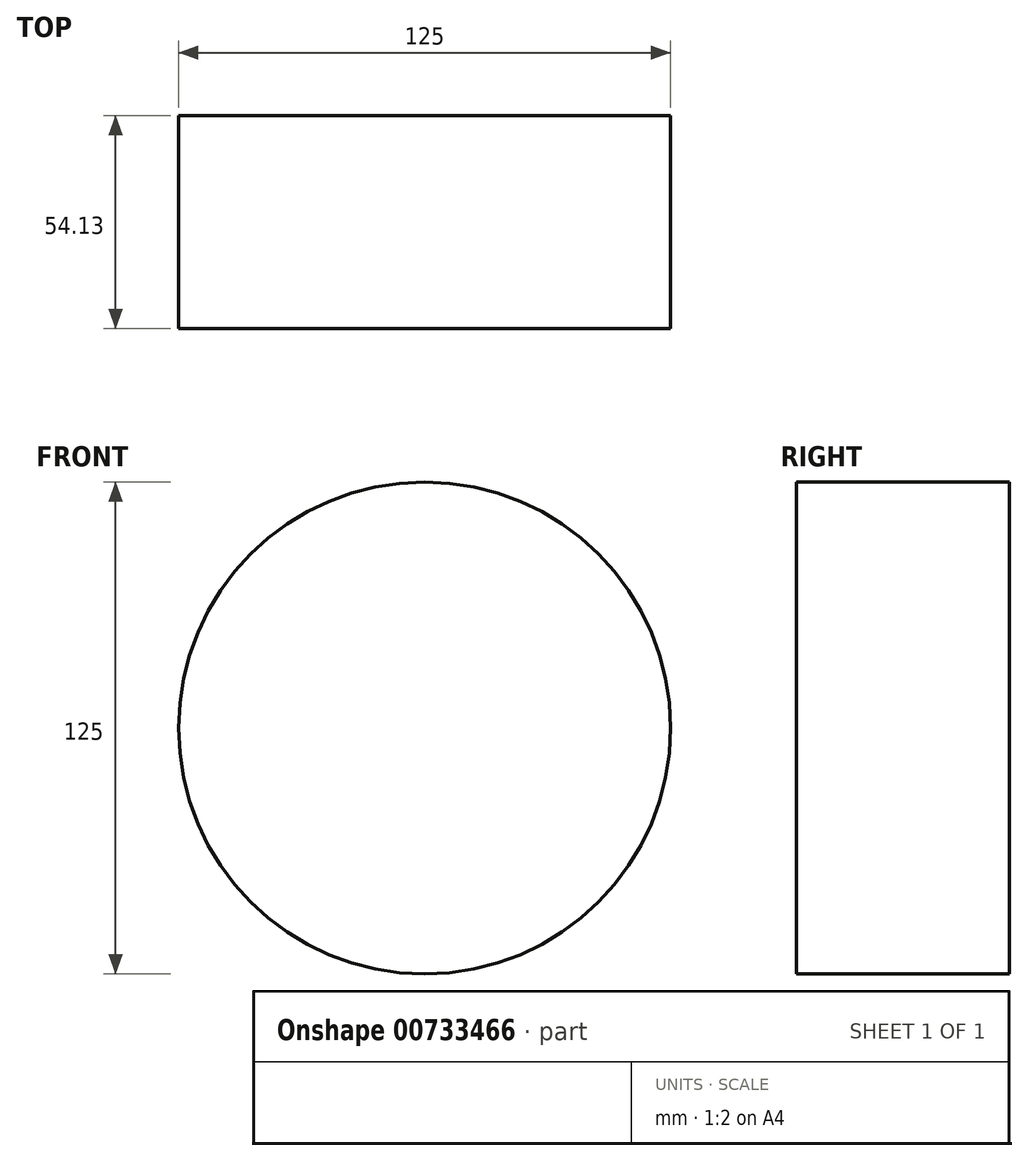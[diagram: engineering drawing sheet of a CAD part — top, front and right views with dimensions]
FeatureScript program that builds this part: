
annotation { "Feature Type Name" : "Feature", "Feature Type Description" : "" }
export const myFeature = defineFeature(function(context is Context, id is Id, definition is map)
    precondition{}
    {
        {
            var Q0;
            Q0=qCreatedBy(makeId("Front.planeOp"),FACE);
            var sketch = newSketch(context, id + "F0", { "sketchPlane" : qUnion([Q0])});
            skCircle(sketch, "E0", {"center": v(-24.71, 27.32) * mm, "radius": 62.5 * mm});
            skSolve(sketch);
        }
        {
            var Q0;
            Q0=makeQuery(id+"F0.imprint","IMPRINT",FACE,{"disambiguationData":[TD([[makeQuery(id+"F0.imprint","IMPRINT",EDGE,{"derivedFrom":sQuery(id+"F0.wireOp",EDGE,"E0")}),1.0]])]});
            extrude(context, id + "F1", {"entities" : qUnion([Q0]), "depth" : 54.13 * mm, "offsetDistance" : 25.4 * mm});
        }
    });
